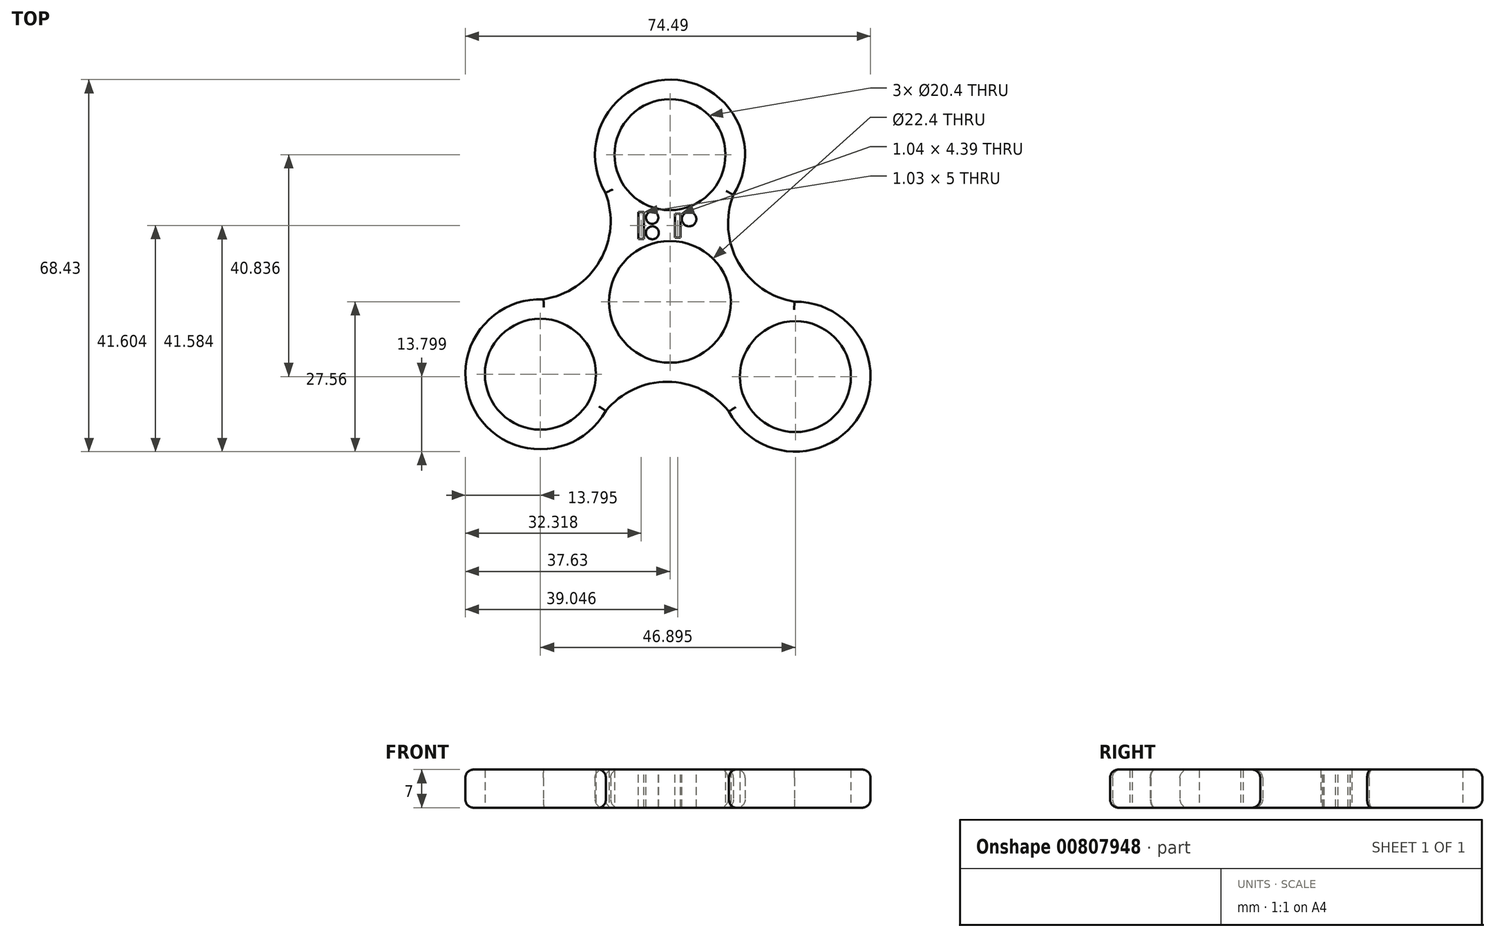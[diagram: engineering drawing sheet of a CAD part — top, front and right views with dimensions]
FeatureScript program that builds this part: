
annotation { "Feature Type Name" : "Feature", "Feature Type Description" : "" }
export const myFeature = defineFeature(function(context is Context, id is Id, definition is map)
    precondition{}
    {
        {
            var Q0;
            Q0=qCreatedBy(makeId("Top.planeOp"),FACE);
            var sketch = newSketch(context, id + "F0", { "sketchPlane" : qUnion([Q0])});
            skCircle(sketch, "E0", {"center": v(0, 0) * mm, "radius": 11.2 * mm});
            skCircle(sketch, "E1", {"center": v(0, 27.07) * mm, "radius": 10.2 * mm});
            skArc(sketch, "E2", {"start": v(11.66, 19.7) * mm, "mid": v(0.2, 40.87) * mm, "end": v(-11.87, 20.04) * mm});
            skArc(sketch, "E3.1.0", {"start": v(-23.27, 0.47) * mm, "mid": v(-35.89, -20.04) * mm, "end": v(-11.8, -20.08) * mm});
            skCircle(sketch, "E3.1.1", {"center": v(-23.83, -13.31) * mm, "radius": 10.2 * mm});
            skArc(sketch, "E3.2.0", {"start": v(10.84, -20.17) * mm, "mid": v(34.9, -20.84) * mm, "end": v(22.9, 0.04) * mm});
            skCircle(sketch, "E3.2.1", {"center": v(23.06, -13.76) * mm, "radius": 10.2 * mm});
            skPoint(sketch, "E3.center", {"position": v(-0.26, 0) * mm});
            skArc(sketch, "E4", {"start": v(12.88, 22.13) * mm, "mid": v(11.97, 8.4) * mm, "end": v(22.9, 0.04) * mm});
            skArc(sketch, "E5.1.0", {"start": v(-26, 0.32) * mm, "mid": v(-13.64, 6.39) * mm, "end": v(-11.87, 20.04) * mm});
            skArc(sketch, "E5.2.0", {"start": v(12.34, -22.45) * mm, "mid": v(0.9, -14.79) * mm, "end": v(-11.8, -20.08) * mm});
            skSolve(sketch);
        }
        {
            var Q0;
            Q0=qSketchRegion(id+"F0",true);
            extrude(context, id + "F1", {"entities" : qUnion([Q0]), "depth" : 7 * mm, "offsetDistance" : 25 * mm});
        }
        {
            var Q0;
            Q0=makeQuery(id+"F1.opExtrude","CAP_EDGE",EDGE,{"disambiguationData":[OSD([sQuery(id+"F0.wireOp",EDGE,"E2")])],"isStart":false});
            var Q1;
            Q1=makeQuery(id+"F1.opExtrude","CAP_EDGE",EDGE,{"disambiguationData":[OSD([sQuery(id+"F0.wireOp",EDGE,"E5.1.0")])],"isStart":false});
            var Q2;
            Q2=makeQuery(id+"F1.opExtrude","CAP_EDGE",EDGE,{"disambiguationData":[OSD([sQuery(id+"F0.wireOp",EDGE,"E3.1.0")])],"isStart":false});
            var Q3;
            Q3=makeQuery(id+"F1.opExtrude","CAP_EDGE",EDGE,{"disambiguationData":[OSD([sQuery(id+"F0.wireOp",EDGE,"E5.2.0")])],"isStart":false});
            var Q4;
            Q4=makeQuery(id+"F1.opExtrude","CAP_EDGE",EDGE,{"disambiguationData":[OSD([sQuery(id+"F0.wireOp",EDGE,"E3.2.0")])],"isStart":false});
            var Q5;
            Q5=makeQuery(id+"F1.opExtrude","CAP_EDGE",EDGE,{"disambiguationData":[OSD([sQuery(id+"F0.wireOp",EDGE,"E4")])],"isStart":false});
            var Q6;
            Q6=makeQuery(id+"F1.opExtrude","CAP_EDGE",EDGE,{"disambiguationData":[OSD([sQuery(id+"F0.wireOp",EDGE,"E2")])],"isStart":true});
            var Q7;
            Q7=makeQuery(id+"F1.opExtrude","CAP_EDGE",EDGE,{"disambiguationData":[OSD([sQuery(id+"F0.wireOp",EDGE,"E5.1.0")])],"isStart":true});
            var Q8;
            Q8=makeQuery(id+"F1.opExtrude","CAP_EDGE",EDGE,{"disambiguationData":[OSD([sQuery(id+"F0.wireOp",EDGE,"E3.1.0")])],"isStart":true});
            var Q9;
            Q9=makeQuery(id+"F1.opExtrude","CAP_EDGE",EDGE,{"disambiguationData":[OSD([sQuery(id+"F0.wireOp",EDGE,"E5.2.0")])],"isStart":true});
            var Q10;
            Q10=makeQuery(id+"F1.opExtrude","CAP_EDGE",EDGE,{"disambiguationData":[OSD([sQuery(id+"F0.wireOp",EDGE,"E3.2.0")])],"isStart":true});
            var Q11;
            Q11=makeQuery(id+"F1.opExtrude","CAP_EDGE",EDGE,{"disambiguationData":[OSD([sQuery(id+"F0.wireOp",EDGE,"E4")])],"isStart":true});
            fillet(context, id + "F2", {"entities" : qUnion([Q0, Q1, Q2, Q3, Q4, Q5, Q6, Q7, Q8, Q9, Q10, Q11]), "radius" : 1.5 * mm, "tangentPropagation" : true, "allowEdgeOverflow" : false});
        }
        {
            var Q0;
            Q0=makeQuery(id+"F1.opExtrude","CAP_FACE",FACE,{"disambiguationData":[OSD([sQuery(id+"F0.wireOp",EDGE,"E0"),sQuery(id+"F0.wireOp",EDGE,"E1"),sQuery(id+"F0.wireOp",EDGE,"E2"),sQuery(id+"F0.wireOp",EDGE,"E3.1.0"),sQuery(id+"F0.wireOp",EDGE,"E3.1.1"),sQuery(id+"F0.wireOp",EDGE,"E3.2.0"),sQuery(id+"F0.wireOp",EDGE,"E3.2.1"),sQuery(id+"F0.wireOp",EDGE,"E4"),sQuery(id+"F0.wireOp",EDGE,"E5.1.0"),sQuery(id+"F0.wireOp",EDGE,"E5.2.0")])],"isStart":false});
            var sketch = newSketch(context, id + "F3", { "sketchPlane" : qUnion([Q0])});
            skLineSegment(sketch, "E6.bottom", {"start": v(-5.83, 16.54) * mm, "end": v(-4.8, 16.54) * mm});
            skLineSegment(sketch, "E6.top", {"start": v(-5.83, 11.54) * mm, "end": v(-4.8, 11.54) * mm});
            skLineSegment(sketch, "E6.left", {"start": v(-5.83, 16.54) * mm, "end": v(-5.83, 11.54) * mm});
            skLineSegment(sketch, "E6.right", {"start": v(-4.8, 16.54) * mm, "end": v(-4.8, 11.54) * mm});
            skCircle(sketch, "E7", {"center": v(-3.28, 15.49) * mm, "radius": 1.13 * mm});
            skCircle(sketch, "E8", {"center": v(-3.24, 12.7) * mm, "radius": 1.19 * mm});
            skLineSegment(sketch, "E9.bottom", {"start": v(0.9, 16.22) * mm, "end": v(1.94, 16.22) * mm});
            skLineSegment(sketch, "E9.top", {"start": v(0.9, 11.83) * mm, "end": v(1.94, 11.83) * mm});
            skLineSegment(sketch, "E9.left", {"start": v(0.9, 16.22) * mm, "end": v(0.9, 11.83) * mm});
            skLineSegment(sketch, "E9.right", {"start": v(1.94, 16.22) * mm, "end": v(1.94, 11.83) * mm});
            skCircle(sketch, "E10", {"center": v(3.5, 15.22) * mm, "radius": 1.33 * mm});
            skSolve(sketch);
        }
        {
            var Q0;
            Q0=makeQuery(id+"F3.imprint","IMPRINT",FACE,{"disambiguationData":[TD([[makeQuery(id+"F3.imprint","IMPRINT",EDGE,{"derivedFrom":sQuery(id+"F3.wireOp",EDGE,"E6.bottom")}),-1.0]])]});
            var Q1;
            Q1=makeQuery(id+"F3.imprint","IMPRINT",FACE,{"disambiguationData":[TD([[makeQuery(id+"F3.imprint","IMPRINT",EDGE,{"derivedFrom":sQuery(id+"F3.wireOp",EDGE,"E7")}),1.0]])]});
            var Q2;
            Q2=makeQuery(id+"F3.imprint","IMPRINT",FACE,{"disambiguationData":[TD([[makeQuery(id+"F3.imprint","IMPRINT",EDGE,{"derivedFrom":sQuery(id+"F3.wireOp",EDGE,"E8")}),1.0]])]});
            var Q3;
            Q3=makeQuery(id+"F3.imprint","IMPRINT",FACE,{"disambiguationData":[TD([[makeQuery(id+"F3.imprint","IMPRINT",EDGE,{"derivedFrom":sQuery(id+"F3.wireOp",EDGE,"E9.bottom")}),-1.0]])]});
            var Q4;
            Q4=makeQuery(id+"F3.imprint","IMPRINT",FACE,{"disambiguationData":[TD([[makeQuery(id+"F3.imprint","IMPRINT",EDGE,{"derivedFrom":sQuery(id+"F3.wireOp",EDGE,"E10")}),1.0]])]});
            extrude(context, id + "F4", {"entities" : qUnion([Q0, Q1, Q2, Q3, Q4]), "operationType" : NewBodyOperationType.REMOVE, "oppositeDirection" : true, "depth" : 25 * mm, "offsetDistance" : 25 * mm});
        }
    });
